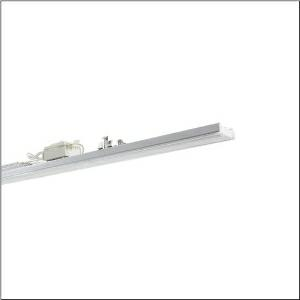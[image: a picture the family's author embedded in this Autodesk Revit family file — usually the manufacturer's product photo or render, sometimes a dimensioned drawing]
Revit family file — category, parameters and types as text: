
# Revit family: licross_r__21_recessed_ho_52tl18mn4e5m_adf3
name_source: partatom
category: Lighting Fixtures
units: mm (PartAtom-declared; Revit-internal decimal feet)

## family parameters
Cut with Voids When Loaded = No
Host = Face
Light Source = No
Part Type = Normal
Room Calculation Point = No
Round Connector Dimension = Use Diameter
Shared = No

## types (1)
- --- (1 x LED, 14940 lm, 83.1 W, 4000K)
    Apparent Load = 83 VA
    CIE Flux Codes = 75 94 99 100 100
    Color Rendering = 80
    Color Temperature = 4000K
    Default Elevation = 1800 mm
    Description = Licross® 21 Recessed HO, luminaire insert, of sheet steel, galvanised, coil coated, white, length: 1.500mm, width: 66mm, height: 67mm, LED rated luminous flux: 14.940lm, light colour: 840, control gear: ON/OFF Multilumen, with plug, 3-pole, with phase selection, mains connection: 220..240V, AC, 50/60Hz, rated input power: 83W, internal wiring halogen-free, primary light control with lens, of plastic, primary optical cover: cover, of PMMA, light emission: direct distribution, primary light characteristic: symmetric, protection rating (complete): IP40, insulation class (complete): insulation class I (protective earthing), certification: CE, ENEC, VDE, UKCA, protection symbol: D if used in an environment without relevant dust loads with corresponding accessories, impact resistance: IK06, permissible ambient temperature for indoor applications: -35..+30°C, corresponds to IFS (International Featured Standards) requirements for safety and quality in the food industry, reducing of maximum allowable ambient temperature of 5°C with ceiling mounting, LABS conformity tested according to VDMA 24364:2018-05, packaging unit: 1 piece
    Height = 58 mm
    Lamp = 1 x LED
    Lamp Light Flux = 14940 lm
    Lamp Power = 83.1 W
    Lamp count = 1
    Length = 1500 mm
    Luminous efficacy = 180 lm/W
    Manufacturer = Siteco
    ModVariant = No
    Model = 52TL18MN4E5M
    Mounting Place = Ceiling
    Mounting Type = Pendant
    Number of Poles = 1
    OnlyDefault = Yes
    Power Factor = 1
    Product Name = Licross® 21 Recessed HO
    Product group = luminaire insert | ceiling pendant
    ProductGroupID = 902
    Protection Class = Protection class I
    Protection Degree = IP 40
    RLX_Detail_Level = 1
    RLX_Emergency_Light_Flux = 0 lm
    RLX_Emergency_Type = 0
    RLX_Emergency_Type_DB = No
    RlxData = <blob elided: 22285 chars, md5=05a9d11c>
    Socket = socket
    Standby Power = 0 W
    System Light Flux = 14940 lm
    System Power = 83 W
    Type Comments = factory setting: luminous flux: 100 % | (A | C | E) | 195 mA
    Type Image = l_1296930.jpg
    URL = http://relux.com
    VarID = @adj_129419
    Voltage = 0 V
    Weight = 0.00 kg
    Width = 66 mm

## geometry (parser evidence)
native form markers: Blend x4, Sweep x12
no freeform markers — native parametric forms only
